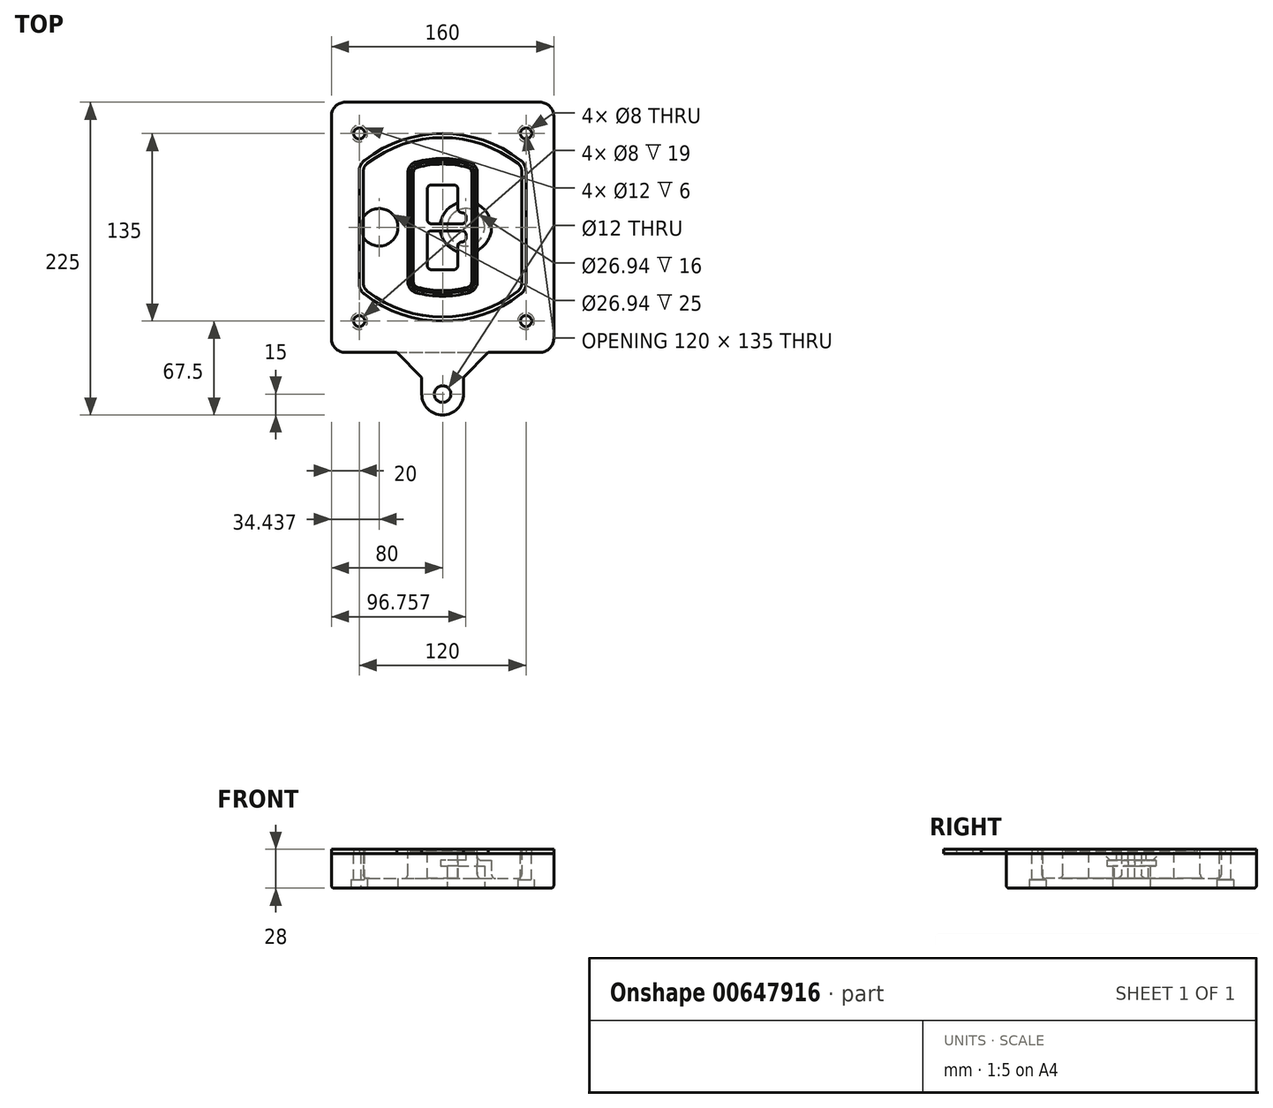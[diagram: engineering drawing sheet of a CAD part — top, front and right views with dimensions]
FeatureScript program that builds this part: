
annotation { "Feature Type Name" : "Feature", "Feature Type Description" : "" }
export const myFeature = defineFeature(function(context is Context, id is Id, definition is map)
    precondition{}
    {
        {
            var Q0;
            Q0=qCreatedBy(makeId("Top.planeOp"),FACE);
            var sketch = newSketch(context, id + "F0", { "sketchPlane" : qUnion([Q0])});
            skPoint(sketch, "E0.rect.middle", {"position": v(0, 0) * mm});
            skLineSegment(sketch, "E1.bottom", {"start": v(-70, -90) * mm, "end": v(70, -90) * mm});
            skLineSegment(sketch, "E1.top", {"start": v(-70, 90) * mm, "end": v(70, 90) * mm});
            skLineSegment(sketch, "E1.left", {"start": v(-80, -80) * mm, "end": v(-80, 80) * mm});
            skLineSegment(sketch, "E1.right", {"start": v(80, -80) * mm, "end": v(80, 80) * mm});
            skLineSegment(sketch, "E2", {"start": v(-80, 90) * mm, "end": v(80, -90) * mm, "construction": true});
            skLineSegment(sketch, "E3", {"start": v(80, 90) * mm, "end": v(-80, -90) * mm, "construction": true});
            skCircle(sketch, "E4", {"center": v(-60, 67.5) * mm, "radius": 4 * mm});
            skCircle(sketch, "E5", {"center": v(60, 67.5) * mm, "radius": 4 * mm});
            skCircle(sketch, "E6", {"center": v(60, -67.5) * mm, "radius": 4 * mm});
            skCircle(sketch, "E7", {"center": v(-60, -67.5) * mm, "radius": 4 * mm});
            skLineSegment(sketch, "E8", {"start": v(-60, 67.5) * mm, "end": v(60, 67.5) * mm, "construction": true});
            skLineSegment(sketch, "E9", {"start": v(60, 67.5) * mm, "end": v(60, -67.5) * mm, "construction": true});
            skLineSegment(sketch, "E10", {"start": v(60, -67.5) * mm, "end": v(-60, -67.5) * mm, "construction": true});
            skLineSegment(sketch, "E11", {"start": v(-60, -67.5) * mm, "end": v(-60, 67.5) * mm, "construction": true});
            skLineSegment(sketch, "E12", {"start": v(-60, 40.3) * mm, "end": v(-60, -40.3) * mm});
            skLineSegment(sketch, "E13", {"start": v(60, 40.3) * mm, "end": v(60, -40.3) * mm});
            skArc(sketch, "E14", {"start": v(56.15, 48.18) * mm, "mid": v(0, 67.5) * mm, "end": v(-56.15, 48.18) * mm});
            skArc(sketch, "E15", {"start": v(-56.15, -48.18) * mm, "mid": v(0, -67.5) * mm, "end": v(56.15, -48.18) * mm});
            skLineSegment(sketch, "E16", {"start": v(-60, 0) * mm, "end": v(60, 0) * mm, "construction": true});
            skPoint(sketch, "E17.visualSharp", {"position": v(-60, -45) * mm});
            skArc(sketch, "E17.filletArc", {"start": v(-60, -40.3) * mm, "mid": v(-58.99, -44.68) * mm, "end": v(-56.15, -48.18) * mm});
            skPoint(sketch, "E18.visualSharp", {"position": v(-60, 45) * mm});
            skArc(sketch, "E18.filletArc", {"start": v(-56.15, 48.18) * mm, "mid": v(-58.99, 44.68) * mm, "end": v(-60, 40.3) * mm});
            skPoint(sketch, "E19.visualSharp", {"position": v(60, 45) * mm});
            skArc(sketch, "E19.filletArc", {"start": v(60, 40.3) * mm, "mid": v(58.99, 44.68) * mm, "end": v(56.15, 48.18) * mm});
            skPoint(sketch, "E20.visualSharp", {"position": v(60, -45) * mm});
            skArc(sketch, "E20.filletArc", {"start": v(56.15, -48.18) * mm, "mid": v(58.99, -44.68) * mm, "end": v(60, -40.3) * mm});
            skPoint(sketch, "E21.visualSharp", {"position": v(-80, 90) * mm});
            skArc(sketch, "E21.filletArc", {"start": v(-70, 90) * mm, "mid": v(-77.07, 87.07) * mm, "end": v(-80, 80) * mm});
            skPoint(sketch, "E22.visualSharp", {"position": v(80, 90) * mm});
            skArc(sketch, "E22.filletArc", {"start": v(80, 80) * mm, "mid": v(77.07, 87.07) * mm, "end": v(70, 90) * mm});
            skPoint(sketch, "E23.visualSharp", {"position": v(80, -90) * mm});
            skArc(sketch, "E23.filletArc", {"start": v(70, -90) * mm, "mid": v(77.07, -87.07) * mm, "end": v(80, -80) * mm});
            skPoint(sketch, "E24.visualSharp", {"position": v(-80, -90) * mm});
            skArc(sketch, "E24.filletArc", {"start": v(-80, -80) * mm, "mid": v(-77.07, -87.07) * mm, "end": v(-70, -90) * mm});
            skArc(sketch, "E25.0", {"start": v(57, 40.3) * mm, "mid": v(56.3, 43.36) * mm, "end": v(54.3, 45.81) * mm});
            skLineSegment(sketch, "E25.1", {"start": v(57, 40.3) * mm, "end": v(57, -40.3) * mm});
            skArc(sketch, "E25.2", {"start": v(54.3, -45.81) * mm, "mid": v(56.3, -43.36) * mm, "end": v(57, -40.3) * mm});
            skArc(sketch, "E25.3", {"start": v(-54.3, -45.81) * mm, "mid": v(0, -64.5) * mm, "end": v(54.3, -45.81) * mm});
            skArc(sketch, "E25.4", {"start": v(-57, -40.3) * mm, "mid": v(-56.3, -43.36) * mm, "end": v(-54.3, -45.81) * mm});
            skArc(sketch, "E25.5", {"start": v(54.3, 45.81) * mm, "mid": v(0, 64.5) * mm, "end": v(-54.3, 45.81) * mm});
            skLineSegment(sketch, "E25.6", {"start": v(-57, 40.3) * mm, "end": v(-57, -40.3) * mm});
            skArc(sketch, "E25.7", {"start": v(-54.3, 45.81) * mm, "mid": v(-56.3, 43.36) * mm, "end": v(-57, 40.3) * mm});
            skArc(sketch, "E26.0", {"start": v(-58.62, 51.33) * mm, "mid": v(-62.58, 46.43) * mm, "end": v(-64, 40.3) * mm});
            skArc(sketch, "E26.1", {"start": v(58.62, 51.33) * mm, "mid": v(0, 71.5) * mm, "end": v(-58.62, 51.33) * mm});
            skArc(sketch, "E26.2", {"start": v(64, 40.3) * mm, "mid": v(62.58, 46.43) * mm, "end": v(58.62, 51.33) * mm});
            skLineSegment(sketch, "E26.3", {"start": v(64, 40.3) * mm, "end": v(64, -40.3) * mm});
            skArc(sketch, "E26.4", {"start": v(58.62, -51.33) * mm, "mid": v(62.58, -46.43) * mm, "end": v(64, -40.3) * mm});
            skLineSegment(sketch, "E26.5", {"start": v(-64, 40.3) * mm, "end": v(-64, -40.3) * mm});
            skArc(sketch, "E26.6", {"start": v(-58.62, -51.33) * mm, "mid": v(0, -71.5) * mm, "end": v(58.62, -51.33) * mm});
            skArc(sketch, "E26.7", {"start": v(-64, -40.3) * mm, "mid": v(-62.58, -46.43) * mm, "end": v(-58.62, -51.33) * mm});
            skSolve(sketch);
        }
        {
            var Q0;
            Q0=makeQuery(id+"F0.imprint","IMPRINT",FACE,{"disambiguationData":[TD([[makeQuery(id+"F0.imprint","IMPRINT",EDGE,{"derivedFrom":sQuery(id+"F0.wireOp",EDGE,"E1.bottom")}),1.0]])]});
            var Q1;
            Q1=makeQuery(id+"F0.imprint","IMPRINT",FACE,{"disambiguationData":[TD([[makeQuery(id+"F0.imprint","IMPRINT",EDGE,{"derivedFrom":sQuery(id+"F0.wireOp",EDGE,"E12")}),1.0]])]});
            var Q2;
            Q2=makeQuery(id+"F0.imprint","IMPRINT",FACE,{"disambiguationData":[TD([[makeQuery(id+"F0.imprint","IMPRINT",EDGE,{"derivedFrom":sQuery(id+"F0.wireOp",EDGE,"E25.0")}),1.0]])]});
            var Q3;
            Q3=makeQuery(id+"F0.imprint","IMPRINT",FACE,{"disambiguationData":[TD([[makeQuery(id+"F0.imprint","IMPRINT",EDGE,{"derivedFrom":sQuery(id+"F0.wireOp",EDGE,"E12")}),-1.0]])]});
            extrude(context, id + "F1", {"entities" : qUnion([Q0, Q1, Q2, Q3]), "oppositeDirection" : true, "depth" : 25 * mm});
        }
        {
            var Q0;
            Q0=makeQuery(id+"F0.imprint","IMPRINT",FACE,{"disambiguationData":[TD([[makeQuery(id+"F0.imprint","IMPRINT",EDGE,{"derivedFrom":sQuery(id+"F0.wireOp",EDGE,"E12")}),1.0]])]});
            extrude(context, id + "F2", {"entities" : qUnion([Q0]), "operationType" : NewBodyOperationType.ADD, "depth" : 3 * mm});
        }
        {
            var Q0;
            Q0=makeQuery(id+"F0.imprint","IMPRINT",FACE,{"disambiguationData":[TD([[makeQuery(id+"F0.imprint","IMPRINT",EDGE,{"derivedFrom":sQuery(id+"F0.wireOp",EDGE,"E25.0")}),1.0]])]});
            extrude(context, id + "F3", {"entities" : qUnion([Q0]), "operationType" : NewBodyOperationType.REMOVE, "oppositeDirection" : true, "depth" : 18 * mm});
        }
        {
            var Q0;
            Q0=makeQuery(id+"F2.opExtrude","CAP_FACE",FACE,{"disambiguationData":[OSD([sQuery(id+"F0.wireOp",EDGE,"E12"),sQuery(id+"F0.wireOp",EDGE,"E13"),sQuery(id+"F0.wireOp",EDGE,"E14"),sQuery(id+"F0.wireOp",EDGE,"E15"),sQuery(id+"F0.wireOp",EDGE,"E17.filletArc"),sQuery(id+"F0.wireOp",EDGE,"E18.filletArc"),sQuery(id+"F0.wireOp",EDGE,"E19.filletArc"),sQuery(id+"F0.wireOp",EDGE,"E20.filletArc"),sQuery(id+"F0.wireOp",EDGE,"E25.0"),sQuery(id+"F0.wireOp",EDGE,"E25.1"),sQuery(id+"F0.wireOp",EDGE,"E25.2"),sQuery(id+"F0.wireOp",EDGE,"E25.3"),sQuery(id+"F0.wireOp",EDGE,"E25.4"),sQuery(id+"F0.wireOp",EDGE,"E25.5"),sQuery(id+"F0.wireOp",EDGE,"E25.6"),sQuery(id+"F0.wireOp",EDGE,"E25.7")])],"isStart":false});
            var sketch = newSketch(context, id + "F4", { "sketchPlane" : qUnion([Q0])});
            skArc(sketch, "E27.0", {"start": v(-19.08, -46.97) * mm, "mid": v(0, -49.5) * mm, "end": v(19.08, -46.97) * mm});
            skArc(sketch, "E28.0", {"start": v(19.08, 46.97) * mm, "mid": v(0, 49.5) * mm, "end": v(-19.08, 46.97) * mm});
            skLineSegment(sketch, "E29", {"start": v(-25, 39.25) * mm, "end": v(-25, -39.25) * mm});
            skLineSegment(sketch, "E30", {"start": v(25, 39.25) * mm, "end": v(25, -39.25) * mm});
            skLineSegment(sketch, "E31", {"start": v(-25, 45.1) * mm, "end": v(25, 45.1) * mm, "construction": true});
            skLineSegment(sketch, "E32", {"start": v(-25, -45.1) * mm, "end": v(25, -45.1) * mm, "construction": true});
            skPoint(sketch, "E33.visualSharp", {"position": v(-25, 45.1) * mm});
            skArc(sketch, "E33.filletArc", {"start": v(-19.08, 46.97) * mm, "mid": v(-23.35, 44.11) * mm, "end": v(-25, 39.25) * mm});
            skPoint(sketch, "E34.visualSharp", {"position": v(25, 45.1) * mm});
            skArc(sketch, "E34.filletArc", {"start": v(25, 39.25) * mm, "mid": v(23.35, 44.11) * mm, "end": v(19.08, 46.97) * mm});
            skPoint(sketch, "E35.visualSharp", {"position": v(25, -45.1) * mm});
            skArc(sketch, "E35.filletArc", {"start": v(19.08, -46.97) * mm, "mid": v(23.35, -44.11) * mm, "end": v(25, -39.25) * mm});
            skPoint(sketch, "E36.visualSharp", {"position": v(-25, -45.1) * mm});
            skArc(sketch, "E36.filletArc", {"start": v(-25, -39.25) * mm, "mid": v(-23.35, -44.11) * mm, "end": v(-19.08, -46.97) * mm});
            skArc(sketch, "E37.0", {"start": v(54.3, 45.81) * mm, "mid": v(0, 64.5) * mm, "end": v(-54.3, 45.81) * mm});
            skArc(sketch, "E37.1", {"start": v(-54.3, 45.81) * mm, "mid": v(-56.3, 43.36) * mm, "end": v(-57, 40.3) * mm});
            skLineSegment(sketch, "E37.2", {"start": v(-57, 40.3) * mm, "end": v(-57, -40.3) * mm});
            skArc(sketch, "E37.3", {"start": v(-57, -40.3) * mm, "mid": v(-56.3, -43.36) * mm, "end": v(-54.3, -45.81) * mm});
            skArc(sketch, "E37.4", {"start": v(-54.3, -45.81) * mm, "mid": v(0, -64.5) * mm, "end": v(54.3, -45.81) * mm});
            skArc(sketch, "E37.5", {"start": v(54.3, -45.81) * mm, "mid": v(56.3, -43.36) * mm, "end": v(57, -40.3) * mm});
            skLineSegment(sketch, "E37.6", {"start": v(57, 40.3) * mm, "end": v(57, -40.3) * mm});
            skArc(sketch, "E37.7", {"start": v(57, 40.3) * mm, "mid": v(56.3, 43.36) * mm, "end": v(54.3, 45.81) * mm});
            skLineSegment(sketch, "E38.0", {"start": v(23, 39.25) * mm, "end": v(23, -39.25) * mm});
            skArc(sketch, "E38.1", {"start": v(18.56, -45.04) * mm, "mid": v(21.76, -42.9) * mm, "end": v(23, -39.25) * mm});
            skArc(sketch, "E38.2", {"start": v(-18.56, -45.04) * mm, "mid": v(0, -47.5) * mm, "end": v(18.56, -45.04) * mm});
            skArc(sketch, "E38.3", {"start": v(-23, -39.25) * mm, "mid": v(-21.76, -42.9) * mm, "end": v(-18.56, -45.04) * mm});
            skLineSegment(sketch, "E38.4", {"start": v(-23, 39.25) * mm, "end": v(-23, -39.25) * mm});
            skArc(sketch, "E38.5", {"start": v(23, 39.25) * mm, "mid": v(21.76, 42.9) * mm, "end": v(18.56, 45.04) * mm});
            skArc(sketch, "E38.6", {"start": v(-18.56, 45.04) * mm, "mid": v(-21.76, 42.9) * mm, "end": v(-23, 39.25) * mm});
            skArc(sketch, "E38.7", {"start": v(18.56, 45.04) * mm, "mid": v(0, 47.5) * mm, "end": v(-18.56, 45.04) * mm});
            skArc(sketch, "E39.0", {"start": v(21, 39.25) * mm, "mid": v(20.18, 41.68) * mm, "end": v(18.04, 43.1) * mm});
            skLineSegment(sketch, "E39.1", {"start": v(21, 39.25) * mm, "end": v(21, -39.25) * mm});
            skArc(sketch, "E39.2", {"start": v(18.04, -43.1) * mm, "mid": v(20.18, -41.68) * mm, "end": v(21, -39.25) * mm});
            skArc(sketch, "E39.3", {"start": v(-18.04, -43.1) * mm, "mid": v(0, -45.5) * mm, "end": v(18.04, -43.1) * mm});
            skArc(sketch, "E39.4", {"start": v(-21, -39.25) * mm, "mid": v(-20.18, -41.68) * mm, "end": v(-18.04, -43.1) * mm});
            skArc(sketch, "E39.5", {"start": v(18.04, 43.1) * mm, "mid": v(0, 45.5) * mm, "end": v(-18.04, 43.1) * mm});
            skLineSegment(sketch, "E39.6", {"start": v(-21, 39.25) * mm, "end": v(-21, -39.25) * mm});
            skArc(sketch, "E39.7", {"start": v(-18.04, 43.1) * mm, "mid": v(-20.18, 41.68) * mm, "end": v(-21, 39.25) * mm});
            skLineSegment(sketch, "E40", {"start": v(-25, 0) * mm, "end": v(25, 0) * mm, "construction": true});
            skLineSegment(sketch, "E41", {"start": v(-11, 5.5) * mm, "end": v(-11, 27.5) * mm});
            skLineSegment(sketch, "E42", {"start": v(-8, 30.5) * mm, "end": v(8, 30.5) * mm});
            skLineSegment(sketch, "E43", {"start": v(11, 27.5) * mm, "end": v(11, 13.5) * mm});
            skLineSegment(sketch, "E44", {"start": v(14, 10.5) * mm, "end": v(14, 10.5) * mm});
            skLineSegment(sketch, "E45", {"start": v(17, 7.5) * mm, "end": v(17, 5.5) * mm});
            skLineSegment(sketch, "E46", {"start": v(14, 2.5) * mm, "end": v(-8, 2.5) * mm});
            skPoint(sketch, "E47.visualSharp", {"position": v(-11, 30.5) * mm});
            skArc(sketch, "E47.filletArc", {"start": v(-8, 30.5) * mm, "mid": v(-10.12, 29.62) * mm, "end": v(-11, 27.5) * mm});
            skPoint(sketch, "E48.visualSharp", {"position": v(11, 30.5) * mm});
            skArc(sketch, "E48.filletArc", {"start": v(11, 27.5) * mm, "mid": v(10.12, 29.62) * mm, "end": v(8, 30.5) * mm});
            skPoint(sketch, "E49.visualSharp", {"position": v(11, 10.5) * mm});
            skArc(sketch, "E49.filletArc", {"start": v(11, 13.5) * mm, "mid": v(11.88, 11.38) * mm, "end": v(14, 10.5) * mm});
            skPoint(sketch, "E50.visualSharp", {"position": v(17, 10.5) * mm});
            skArc(sketch, "E50.filletArc", {"start": v(17, 7.5) * mm, "mid": v(16.12, 9.62) * mm, "end": v(14, 10.5) * mm});
            skPoint(sketch, "E51.visualSharp", {"position": v(17, 2.5) * mm});
            skArc(sketch, "E51.filletArc", {"start": v(14, 2.5) * mm, "mid": v(16.12, 3.38) * mm, "end": v(17, 5.5) * mm});
            skPoint(sketch, "E52.visualSharp", {"position": v(-11, 2.5) * mm});
            skArc(sketch, "E52.filletArc", {"start": v(-11, 5.5) * mm, "mid": v(-10.12, 3.38) * mm, "end": v(-8, 2.5) * mm});
            skLineSegment(sketch, "E53.0.MirrorCS", {"start": v(14, -2.5) * mm, "end": v(-8, -2.5) * mm});
            skArc(sketch, "E54.0.MirrorCS", {"start": v(-11, -5.5) * mm, "mid": v(-10.12, -3.38) * mm, "end": v(-8, -2.5) * mm});
            skLineSegment(sketch, "E55.0.MirrorCS", {"start": v(-11, -5.5) * mm, "end": v(-11, -27.5) * mm});
            skArc(sketch, "E56.0.MirrorCS", {"start": v(-8, -30.5) * mm, "mid": v(-10.12, -29.62) * mm, "end": v(-11, -27.5) * mm});
            skLineSegment(sketch, "E57.0.MirrorCS", {"start": v(-8, -30.5) * mm, "end": v(8, -30.5) * mm});
            skArc(sketch, "E58.0.MirrorCS", {"start": v(11, -27.5) * mm, "mid": v(10.12, -29.62) * mm, "end": v(8, -30.5) * mm});
            skLineSegment(sketch, "E59.0.MirrorCS", {"start": v(11, -27.5) * mm, "end": v(11, -13.5) * mm});
            skArc(sketch, "E60.0.MirrorCS", {"start": v(11, -13.5) * mm, "mid": v(11.88, -11.38) * mm, "end": v(14, -10.5) * mm});
            skArc(sketch, "E61.0.MirrorCS", {"start": v(17, -7.5) * mm, "mid": v(16.12, -9.62) * mm, "end": v(14, -10.5) * mm});
            skLineSegment(sketch, "E62.0.MirrorCS", {"start": v(17, -7.5) * mm, "end": v(17, -5.5) * mm});
            skArc(sketch, "E63.0.MirrorCS", {"start": v(14, -2.5) * mm, "mid": v(16.12, -3.38) * mm, "end": v(17, -5.5) * mm});
            skSolve(sketch);
        }
        {
            var Q0;
            Q0=makeQuery(id+"F4.imprint","IMPRINT",FACE,{"disambiguationData":[TD([[makeQuery(id+"F4.imprint","IMPRINT",EDGE,{"derivedFrom":sQuery(id+"F4.wireOp",EDGE,"E27.0")}),1.0]])]});
            var Q1;
            Q1=makeQuery(id+"F4.imprint","IMPRINT",FACE,{"disambiguationData":[TD([[makeQuery(id+"F4.imprint","IMPRINT",EDGE,{"derivedFrom":sQuery(id+"F4.wireOp",EDGE,"E38.0")}),-1.0]])]});
            var Q2;
            Q2=makeQuery(id+"F4.imprint","IMPRINT",FACE,{"disambiguationData":[TD([[makeQuery(id+"F4.imprint","IMPRINT",EDGE,{"derivedFrom":sQuery(id+"F4.wireOp",EDGE,"E39.0")}),1.0]])]});
            extrude(context, id + "F5", {"entities" : qUnion([Q0, Q1, Q2]), "operationType" : NewBodyOperationType.ADD, "endBound" : BoundingType.UP_TO_NEXT, "oppositeDirection" : true, "depth" : 25 * mm});
        }
        {
            var Q0;
            Q0=makeQuery(id+"F4.imprint","IMPRINT",FACE,{"disambiguationData":[TD([[makeQuery(id+"F4.imprint","IMPRINT",EDGE,{"derivedFrom":sQuery(id+"F4.wireOp",EDGE,"E38.0")}),-1.0]])]});
            extrude(context, id + "F6", {"entities" : qUnion([Q0]), "operationType" : NewBodyOperationType.REMOVE, "oppositeDirection" : true, "depth" : 2 * mm});
        }
        {
            var Q0;
            Q0=makeQuery(id+"F1.opExtrude","CAP_FACE",FACE,{"disambiguationData":[OSD([sQuery(id+"F0.wireOp",EDGE,"E1.bottom"),sQuery(id+"F0.wireOp",EDGE,"E1.top"),sQuery(id+"F0.wireOp",EDGE,"E1.left"),sQuery(id+"F0.wireOp",EDGE,"E1.right"),sQuery(id+"F0.wireOp",EDGE,"E4"),sQuery(id+"F0.wireOp",EDGE,"E5"),sQuery(id+"F0.wireOp",EDGE,"E6"),sQuery(id+"F0.wireOp",EDGE,"E7"),sQuery(id+"F0.wireOp",EDGE,"E21.filletArc"),sQuery(id+"F0.wireOp",EDGE,"E22.filletArc"),sQuery(id+"F0.wireOp",EDGE,"E23.filletArc"),sQuery(id+"F0.wireOp",EDGE,"E24.filletArc")])],"isStart":false});
            var sketch = newSketch(context, id + "F7", { "sketchPlane" : qUnion([Q0])});
            skCircle(sketch, "E64", {"center": v(16.76, 0) * mm, "radius": 13.47 * mm});
            skCircle(sketch, "E65", {"center": v(-45.56, 0) * mm, "radius": 13.47 * mm});
            skLineSegment(sketch, "E66", {"start": v(80, 0) * mm, "end": v(-80, 0) * mm});
            skCircle(sketch, "E67", {"center": v(16.76, 0) * mm, "radius": 18.47 * mm});
            skCircle(sketch, "E68", {"center": v(60, -67.5) * mm, "radius": 6 * mm});
            skCircle(sketch, "E69", {"center": v(-60, -67.5) * mm, "radius": 6 * mm});
            skCircle(sketch, "E70", {"center": v(-60, 67.5) * mm, "radius": 6 * mm});
            skCircle(sketch, "E71", {"center": v(60, 67.5) * mm, "radius": 6 * mm});
            skSolve(sketch);
        }
        {
            var Q0;
            {var subQ1=sQuery(id+"F7.wireOp",EDGE,"E66");var subQ4=sQuery(id+"F7.wireOp",EDGE,"E64");var subQ6=makeQuery(id+"F7.imprint","INTERSECT",VERTEX,{"disambiguationData":[OD(0.0)],"derivedFrom":[subQ4,subQ1]});Q0=makeQuery(id+"F7.imprint","IMPRINT",FACE,{"disambiguationData":[TD([[makeQuery(id+"F7.imprint","IMPRINT",EDGE,{"disambiguationData":[TD([[subQ6,-1.0]])],"derivedFrom":subQ4}),-1.0]])]});}
            var Q1;
            {var subQ0=sQuery(id+"F7.wireOp",EDGE,"E66");var subQ1=sQuery(id+"F7.wireOp",EDGE,"E64");var subQ3=makeQuery(id+"F7.imprint","INTERSECT",VERTEX,{"disambiguationData":[OD(0.0)],"derivedFrom":[subQ1,subQ0]});Q1=makeQuery(id+"F7.imprint","IMPRINT",FACE,{"disambiguationData":[TD([[makeQuery(id+"F7.imprint","IMPRINT",EDGE,{"disambiguationData":[TD([[subQ3,-1.0]])],"derivedFrom":subQ1}),1.0]])]});}
            var Q2;
            {var subQ0=sQuery(id+"F7.wireOp",EDGE,"E66");var subQ1=sQuery(id+"F7.wireOp",EDGE,"E64");var subQ3=makeQuery(id+"F7.imprint","INTERSECT",VERTEX,{"disambiguationData":[OD(0.0)],"derivedFrom":[subQ1,subQ0]});Q2=makeQuery(id+"F7.imprint","IMPRINT",FACE,{"disambiguationData":[TD([[makeQuery(id+"F7.imprint","IMPRINT",EDGE,{"disambiguationData":[TD([[subQ3,1.0]])],"derivedFrom":subQ1}),1.0]])]});}
            var Q3;
            {var subQ1=sQuery(id+"F7.wireOp",EDGE,"E66");var subQ4=sQuery(id+"F7.wireOp",EDGE,"E64");var subQ6=makeQuery(id+"F7.imprint","INTERSECT",VERTEX,{"disambiguationData":[OD(0.0)],"derivedFrom":[subQ4,subQ1]});Q3=makeQuery(id+"F7.imprint","IMPRINT",FACE,{"disambiguationData":[TD([[makeQuery(id+"F7.imprint","IMPRINT",EDGE,{"disambiguationData":[TD([[subQ6,1.0]])],"derivedFrom":subQ4}),-1.0]])]});}
            extrude(context, id + "F8", {"entities" : qUnion([Q0, Q1, Q2, Q3]), "operationType" : NewBodyOperationType.ADD, "oppositeDirection" : true, "depth" : 20 * mm});
        }
        {
            var Q0;
            {var subQ0=sQuery(id+"F7.wireOp",EDGE,"E66");var subQ1=sQuery(id+"F7.wireOp",EDGE,"E64");var subQ3=makeQuery(id+"F7.imprint","INTERSECT",VERTEX,{"disambiguationData":[OD(0.0)],"derivedFrom":[subQ1,subQ0]});Q0=makeQuery(id+"F7.imprint","IMPRINT",FACE,{"disambiguationData":[TD([[makeQuery(id+"F7.imprint","IMPRINT",EDGE,{"disambiguationData":[TD([[subQ3,-1.0]])],"derivedFrom":subQ1}),1.0]])]});}
            var Q1;
            {var subQ0=sQuery(id+"F7.wireOp",EDGE,"E66");var subQ1=sQuery(id+"F7.wireOp",EDGE,"E64");var subQ3=makeQuery(id+"F7.imprint","INTERSECT",VERTEX,{"disambiguationData":[OD(0.0)],"derivedFrom":[subQ1,subQ0]});Q1=makeQuery(id+"F7.imprint","IMPRINT",FACE,{"disambiguationData":[TD([[makeQuery(id+"F7.imprint","IMPRINT",EDGE,{"disambiguationData":[TD([[subQ3,1.0]])],"derivedFrom":subQ1}),1.0]])]});}
            extrude(context, id + "F9", {"entities" : qUnion([Q0, Q1]), "operationType" : NewBodyOperationType.REMOVE, "oppositeDirection" : true, "depth" : 16 * mm});
        }
        {
            var Q0;
            {var subQ0=sQuery(id+"F7.wireOp",EDGE,"E66");var subQ1=sQuery(id+"F7.wireOp",EDGE,"E65");var subQ3=makeQuery(id+"F7.imprint","INTERSECT",VERTEX,{"disambiguationData":[OD(0.0)],"derivedFrom":[subQ1,subQ0]});Q0=makeQuery(id+"F7.imprint","IMPRINT",FACE,{"disambiguationData":[TD([[makeQuery(id+"F7.imprint","IMPRINT",EDGE,{"disambiguationData":[TD([[subQ3,-1.0]])],"derivedFrom":subQ1}),1.0]])]});}
            var Q1;
            {var subQ0=sQuery(id+"F7.wireOp",EDGE,"E66");var subQ1=sQuery(id+"F7.wireOp",EDGE,"E65");var subQ3=makeQuery(id+"F7.imprint","INTERSECT",VERTEX,{"disambiguationData":[OD(0.0)],"derivedFrom":[subQ1,subQ0]});Q1=makeQuery(id+"F7.imprint","IMPRINT",FACE,{"disambiguationData":[TD([[makeQuery(id+"F7.imprint","IMPRINT",EDGE,{"disambiguationData":[TD([[subQ3,1.0]])],"derivedFrom":subQ1}),1.0]])]});}
            extrude(context, id + "F10", {"entities" : qUnion([Q0, Q1]), "operationType" : NewBodyOperationType.REMOVE, "oppositeDirection" : true, "depth" : 25 * mm});
        }
        {
            var Q0;
            Q0=makeQuery(id+"F7.imprint","IMPRINT",FACE,{"disambiguationData":[TD([[makeQuery(id+"F7.imprint","IMPRINT",EDGE,{"derivedFrom":sQuery(id+"F7.wireOp",EDGE,"E68")}),1.0]])]});
            var Q1;
            Q1=makeQuery(id+"F7.imprint","IMPRINT",FACE,{"disambiguationData":[TD([[makeQuery(id+"F7.imprint","IMPRINT",EDGE,{"derivedFrom":makeQuery(id+"F1.opExtrude","CAP_EDGE",EDGE,{"disambiguationData":[OSD([sQuery(id+"F0.wireOp",EDGE,"E5")])],"isStart":false})}),-1.0]])]});
            var Q2;
            Q2=makeQuery(id+"F7.imprint","IMPRINT",FACE,{"disambiguationData":[TD([[makeQuery(id+"F7.imprint","IMPRINT",EDGE,{"derivedFrom":sQuery(id+"F7.wireOp",EDGE,"E69")}),1.0]])]});
            var Q3;
            Q3=makeQuery(id+"F7.imprint","IMPRINT",FACE,{"disambiguationData":[TD([[makeQuery(id+"F7.imprint","IMPRINT",EDGE,{"derivedFrom":makeQuery(id+"F1.opExtrude","CAP_EDGE",EDGE,{"disambiguationData":[OSD([sQuery(id+"F0.wireOp",EDGE,"E4")])],"isStart":false})}),-1.0]])]});
            var Q4;
            Q4=makeQuery(id+"F7.imprint","IMPRINT",FACE,{"disambiguationData":[TD([[makeQuery(id+"F7.imprint","IMPRINT",EDGE,{"derivedFrom":sQuery(id+"F7.wireOp",EDGE,"E70")}),1.0]])]});
            var Q5;
            Q5=makeQuery(id+"F7.imprint","IMPRINT",FACE,{"disambiguationData":[TD([[makeQuery(id+"F7.imprint","IMPRINT",EDGE,{"derivedFrom":makeQuery(id+"F1.opExtrude","CAP_EDGE",EDGE,{"disambiguationData":[OSD([sQuery(id+"F0.wireOp",EDGE,"E7")])],"isStart":false})}),-1.0]])]});
            var Q6;
            Q6=makeQuery(id+"F7.imprint","IMPRINT",FACE,{"disambiguationData":[TD([[makeQuery(id+"F7.imprint","IMPRINT",EDGE,{"derivedFrom":sQuery(id+"F7.wireOp",EDGE,"E71")}),1.0]])]});
            var Q7;
            Q7=makeQuery(id+"F7.imprint","IMPRINT",FACE,{"disambiguationData":[TD([[makeQuery(id+"F7.imprint","IMPRINT",EDGE,{"derivedFrom":makeQuery(id+"F1.opExtrude","CAP_EDGE",EDGE,{"disambiguationData":[OSD([sQuery(id+"F0.wireOp",EDGE,"E6")])],"isStart":false})}),-1.0]])]});
            extrude(context, id + "F11", {"entities" : qUnion([Q0, Q1, Q2, Q3, Q4, Q5, Q6, Q7]), "operationType" : NewBodyOperationType.REMOVE, "oppositeDirection" : true, "depth" : 6 * mm});
        }
        {
            var Q0;
            Q0=makeQuery(id+"F9.boolean.opBoolean","COPY",FACE,{"derivedFrom":makeQuery(id+"F9.opExtrude","CAP_FACE",FACE,{"disambiguationData":[OSD([sQuery(id+"F7.wireOp",EDGE,"E64")])],"isStart":false})});
            var sketch = newSketch(context, id + "F12", { "sketchPlane" : qUnion([Q0])});
            skArc(sketch, "E72.0", {"start": v(11, 17.55) * mm, "mid": v(2.57, 11.82) * mm, "end": v(-1.54, 2.5) * mm});
            skArc(sketch, "E72.1", {"start": v(-1.54, -2.5) * mm, "mid": v(2.57, -11.82) * mm, "end": v(11, -17.55) * mm});
            skLineSegment(sketch, "E73", {"start": v(-1.54, -2.5) * mm, "end": v(14, -2.5) * mm});
            skLineSegment(sketch, "E74.0", {"start": v(14, 2.5) * mm, "end": v(-1.54, 2.5) * mm});
            skArc(sketch, "E74.1", {"start": v(14, 2.5) * mm, "mid": v(16.12, 3.38) * mm, "end": v(17, 5.5) * mm});
            skLineSegment(sketch, "E74.2", {"start": v(17, 7.5) * mm, "end": v(17, 5.5) * mm});
            skArc(sketch, "E74.3", {"start": v(17, 7.5) * mm, "mid": v(16.12, 9.62) * mm, "end": v(14, 10.5) * mm});
            skArc(sketch, "E74.4", {"start": v(11, 13.5) * mm, "mid": v(11.88, 11.38) * mm, "end": v(14, 10.5) * mm});
            skLineSegment(sketch, "E74.5", {"start": v(11, 17.55) * mm, "end": v(11, 13.5) * mm});
            skLineSegment(sketch, "E74.7", {"start": v(14, -2.5) * mm, "end": v(-1.54, -2.5) * mm});
            skArc(sketch, "E74.8", {"start": v(14, -2.5) * mm, "mid": v(16.12, -3.38) * mm, "end": v(17, -5.5) * mm});
            skLineSegment(sketch, "E74.9", {"start": v(17, -7.5) * mm, "end": v(17, -5.5) * mm});
            skArc(sketch, "E74.10", {"start": v(17, -7.5) * mm, "mid": v(16.12, -9.62) * mm, "end": v(14, -10.5) * mm});
            skArc(sketch, "E74.11", {"start": v(11, -13.5) * mm, "mid": v(11.88, -11.38) * mm, "end": v(14, -10.5) * mm});
            skLineSegment(sketch, "E74.12", {"start": v(11, -17.55) * mm, "end": v(11, -13.5) * mm});
            skPoint(sketch, "E75.orphan", {"position": v(11, -27.5) * mm});
            skPoint(sketch, "E76.orphan", {"position": v(-8, -2.5) * mm});
            skPoint(sketch, "E77.orphan", {"position": v(-8, 2.5) * mm});
            skPoint(sketch, "E78.orphan", {"position": v(11, 27.5) * mm});
            skSolve(sketch);
        }
        {
            var Q0;
            {var subQ7=sQuery(id+"F12.wireOp",EDGE,"E72.0");var subQ14=sQuery(id+"F12.wireOp",EDGE,"E72.1");var subQ16=sQuery(id+"F12.wireOp",EDGE,"E74.1");var subQ18=sQuery(id+"F12.wireOp",EDGE,"E74.8");Q0=qUnion([makeQuery(id+"F12.imprint","IMPRINT",FACE,{"disambiguationData":[TD([[makeQuery(id+"F12.imprint","IMPRINT",EDGE,{"derivedFrom":subQ7}),1.0]])]}),makeQuery(id+"F12.imprint","IMPRINT",FACE,{"disambiguationData":[TD([[makeQuery(id+"F12.imprint","IMPRINT",EDGE,{"derivedFrom":subQ14}),1.0]])]}),makeQuery(id+"F12.imprint","IMPRINT",FACE,{"disambiguationData":[TD([[makeQuery(id+"F12.imprint","IMPRINT",EDGE,{"derivedFrom":subQ16}),1.0]])]}),makeQuery(id+"F12.imprint","IMPRINT",FACE,{"disambiguationData":[TD([[makeQuery(id+"F12.imprint","IMPRINT",EDGE,{"derivedFrom":subQ18}),-1.0]])]})]);}
            var Q1;
            Q1=makeQuery(id+"F5.boolean.opBoolean","SPLIT",FACE,{"disambiguationData":[TD([makeQuery(id+"F5.opExtrude","SWEPT_FACE",FACE,{"disambiguationData":[OSD([sQuery(id+"F4.wireOp",EDGE,"E41")])]})])],"derivedFrom":makeQuery(id+"F3.boolean.opBoolean","COPY",FACE,{"derivedFrom":makeQuery(id+"F3.opExtrude","CAP_FACE",FACE,{"disambiguationData":[OSD([sQuery(id+"F0.wireOp",EDGE,"E25.0"),sQuery(id+"F0.wireOp",EDGE,"E25.1"),sQuery(id+"F0.wireOp",EDGE,"E25.2"),sQuery(id+"F0.wireOp",EDGE,"E25.3"),sQuery(id+"F0.wireOp",EDGE,"E25.4"),sQuery(id+"F0.wireOp",EDGE,"E25.5"),sQuery(id+"F0.wireOp",EDGE,"E25.6"),sQuery(id+"F0.wireOp",EDGE,"E25.7")])],"isStart":false})})});
            extrude(context, id + "F13", {"entities" : qUnion([Q0]), "operationType" : NewBodyOperationType.REMOVE, "endBound" : BoundingType.UP_TO_SURFACE, "endBoundEntityFace" : qUnion([Q1]), "depth" : 25 * mm});
        }
        {
            var Q0;
            Q0=makeQuery(id+"F3.boolean.opBoolean","COPY",EDGE,{"derivedFrom":makeQuery(id+"F3.opExtrude","CAP_EDGE",EDGE,{"disambiguationData":[OSD([sQuery(id+"F0.wireOp",EDGE,"E25.6")])],"isStart":false})});
            var Q1;
            Q1=makeQuery(id+"F8.boolean.opBoolean","INTERSECT",EDGE,{"derivedFrom":[makeQuery(id+"F5.opExtrude","SWEPT_FACE",FACE,{"disambiguationData":[OSD([sQuery(id+"F4.wireOp",EDGE,"E30")])]}),makeQuery(id+"F8.opExtrude","CAP_FACE",FACE,{"disambiguationData":[OSD([sQuery(id+"F7.wireOp",EDGE,"E67")])],"isStart":false})]});
            var Q2;
            Q2=makeQuery(id+"F8.boolean.opBoolean","INTERSECT",EDGE,{"disambiguationData":[OD(1.0)],"derivedFrom":[makeQuery(id+"F5.opExtrude","SWEPT_FACE",FACE,{"disambiguationData":[OSD([sQuery(id+"F4.wireOp",EDGE,"E30")])]}),makeQuery(id+"F8.opExtrude","SWEPT_FACE",FACE,{"disambiguationData":[OSD([sQuery(id+"F7.wireOp",EDGE,"E67")])]})]});
            var Q3;
            {var subQ0=sQuery(id+"F4.wireOp",EDGE,"E30");Q3=makeQuery(id+"F8.boolean.opBoolean","SPLIT",EDGE,{"disambiguationData":[TD([makeQuery(id+"F5.opExtrude","SWEPT_FACE",FACE,{"disambiguationData":[OSD([sQuery(id+"F4.wireOp",EDGE,"E35.filletArc")])]})])],"derivedFrom":makeQuery(id+"F5.opExtrude","CAP_EDGE",EDGE,{"disambiguationData":[OSD([subQ0])],"isStart":false})});}
            var Q4;
            {var subQ0=sQuery(id+"F0.wireOp",EDGE,"E25.7");var subQ1=sQuery(id+"F0.wireOp",EDGE,"E25.1");var subQ2=sQuery(id+"F0.wireOp",EDGE,"E25.6");var subQ3=sQuery(id+"F0.wireOp",EDGE,"E25.5");var subQ4=sQuery(id+"F0.wireOp",EDGE,"E25.4");var subQ5=sQuery(id+"F0.wireOp",EDGE,"E25.0");var subQ6=sQuery(id+"F0.wireOp",EDGE,"E25.2");var subQ7=sQuery(id+"F0.wireOp",EDGE,"E25.3");Q4=makeQuery(id+"F8.boolean.opBoolean","INTERSECT",EDGE,{"derivedFrom":[makeQuery(id+"F5.boolean.opBoolean","SPLIT",FACE,{"disambiguationData":[TD([makeQuery(id+"F2.opExtrude","SWEPT_FACE",FACE,{"disambiguationData":[OSD([subQ5])]})])],"derivedFrom":makeQuery(id+"F3.boolean.opBoolean","COPY",FACE,{"derivedFrom":makeQuery(id+"F3.opExtrude","CAP_FACE",FACE,{"disambiguationData":[OSD([subQ5,subQ1,subQ6,subQ7,subQ4,subQ3,subQ2,subQ0])],"isStart":false})})}),makeQuery(id+"F8.opExtrude","SWEPT_FACE",FACE,{"disambiguationData":[OSD([sQuery(id+"F7.wireOp",EDGE,"E67")])]})]});}
            var Q5;
            Q5=makeQuery(id+"F8.boolean.opBoolean","INTERSECT",EDGE,{"disambiguationData":[OD(0.0)],"derivedFrom":[makeQuery(id+"F5.opExtrude","SWEPT_FACE",FACE,{"disambiguationData":[OSD([sQuery(id+"F4.wireOp",EDGE,"E30")])]}),makeQuery(id+"F8.opExtrude","SWEPT_FACE",FACE,{"disambiguationData":[OSD([sQuery(id+"F7.wireOp",EDGE,"E67")])]})]});
            fillet(context, id + "F14", {"entities" : qUnion([Q0, Q1, Q2, Q3, Q4, Q5]), "radius" : 3 * mm, "tangentPropagation" : true, "allowEdgeOverflow" : false});
        }
        {
            var Q0;
            Q0=makeQuery(id+"F1.opExtrude","CAP_EDGE",EDGE,{"disambiguationData":[OSD([sQuery(id+"F0.wireOp",EDGE,"E1.bottom")])],"isStart":false});
            fillet(context, id + "F15", {"entities" : qUnion([Q0]), "radius" : 2 * mm, "tangentPropagation" : true, "allowEdgeOverflow" : false});
        }
        {
            var Q0;
            {var subQ0=sQuery(id+"F0.wireOp",EDGE,"E21.filletArc");var subQ1=sQuery(id+"F0.wireOp",EDGE,"E7");var subQ2=sQuery(id+"F0.wireOp",EDGE,"E6");var subQ3=sQuery(id+"F0.wireOp",EDGE,"E5");var subQ4=sQuery(id+"F0.wireOp",EDGE,"E4");var subQ5=sQuery(id+"F0.wireOp",EDGE,"E22.filletArc");var subQ6=sQuery(id+"F0.wireOp",EDGE,"E1.bottom");var subQ7=sQuery(id+"F0.wireOp",EDGE,"E1.right");var subQ8=sQuery(id+"F0.wireOp",EDGE,"E1.top");var subQ9=sQuery(id+"F0.wireOp",EDGE,"E1.left");var subQ10=sQuery(id+"F0.wireOp",EDGE,"E23.filletArc");var subQ11=sQuery(id+"F0.wireOp",EDGE,"E24.filletArc");Q0=makeQuery(id+"F2.boolean.opBoolean","SPLIT",FACE,{"disambiguationData":[TD([makeQuery(id+"F1.opExtrude","SWEPT_FACE",FACE,{"disambiguationData":[OSD([subQ6])]})])],"derivedFrom":makeQuery(id+"F1.opExtrude","CAP_FACE",FACE,{"disambiguationData":[OSD([subQ6,subQ8,subQ9,subQ7,subQ4,subQ3,subQ2,subQ1,subQ0,subQ5,subQ10,subQ11])],"isStart":true})});}
            var sketch = newSketch(context, id + "F16", { "sketchPlane" : qUnion([Q0])});
            skLineSegment(sketch, "E79", {"start": v(-33, 90) * mm, "end": v(-15, 108) * mm});
            skLineSegment(sketch, "E80", {"start": v(-15, 108) * mm, "end": v(-15, 120) * mm});
            skLineSegment(sketch, "E81", {"start": v(0, 90) * mm, "end": v(0, 120) * mm, "construction": true});
            skCircle(sketch, "E82", {"center": v(0, 120) * mm, "radius": 6 * mm});
            skLineSegment(sketch, "E83.MirrorCS", {"start": v(15, 108) * mm, "end": v(15, 120) * mm});
            skLineSegment(sketch, "E84.MirrorCS", {"start": v(33, 90) * mm, "end": v(15, 108) * mm});
            skArc(sketch, "E85", {"start": v(15, 120) * mm, "mid": v(0, 135) * mm, "end": v(-15, 120) * mm});
            skLineSegment(sketch, "E86", {"start": v(-80, 0) * mm, "end": v(80, 0) * mm, "construction": true});
            skArc(sketch, "E87.MirrorCS", {"start": v(-15, 120) * mm, "mid": v(0, 135) * mm, "end": v(15, 120) * mm});
            skLineSegment(sketch, "E88.MirrorCS", {"start": v(80, 0) * mm, "end": v(-80, 0) * mm, "construction": true});
            skLineSegment(sketch, "E89.MirrorCS", {"start": v(-15, -108) * mm, "end": v(-15, -120) * mm});
            skLineSegment(sketch, "E90.MirrorCS", {"start": v(15, -108) * mm, "end": v(15, -120) * mm});
            skCircle(sketch, "E91.MirrorC", {"center": v(0, -120) * mm, "radius": 6 * mm});
            skArc(sketch, "E92.MirrorCS", {"start": v(15, -120) * mm, "mid": v(0, -135) * mm, "end": v(-15, -120) * mm});
            skLineSegment(sketch, "E93.MirrorCS", {"start": v(-33, -90) * mm, "end": v(-15, -108) * mm});
            skLineSegment(sketch, "E94.MirrorCS", {"start": v(33, -90) * mm, "end": v(15, -108) * mm});
            skArc(sketch, "E95.MirrorCS", {"start": v(-15, -120) * mm, "mid": v(0, -135) * mm, "end": v(15, -120) * mm});
            skLineSegment(sketch, "E96.MirrorCS", {"start": v(0, -90) * mm, "end": v(0, -120) * mm, "construction": true});
            skSolve(sketch);
        }
        {
            var Q0;
            {var subQ0=sQuery(id+"F16.wireOp",EDGE,"E94.MirrorCS");Q0=makeQuery(id+"F16.imprint","IMPRINT",FACE,{"disambiguationData":[TD([[makeQuery(id+"F16.imprint","IMPRINT",EDGE,{"derivedFrom":subQ0}),-1.0]])]});}
            var Q1;
            Q1=makeQuery(id+"F16.imprint","IMPRINT",FACE,{"disambiguationData":[TD([[makeQuery(id+"F16.imprint","IMPRINT",EDGE,{"derivedFrom":sQuery(id+"F16.wireOp",EDGE,"E87.MirrorCS")}),-1.0]])]});
            var Q2;
            Q2=makeQuery(id+"F16.imprint","IMPRINT",FACE,{"disambiguationData":[TD([[makeQuery(id+"F16.imprint","IMPRINT",EDGE,{"derivedFrom":makeQuery(id+"F1.opExtrude","CAP_EDGE",EDGE,{"disambiguationData":[OSD([sQuery(id+"F0.wireOp",EDGE,"E1.left")])],"isStart":true})}),-1.0]])]});
            var Q3;
            Q3=makeQuery(id+"F2.opExtrude","CAP_FACE",FACE,{"disambiguationData":[OSD([sQuery(id+"F0.wireOp",EDGE,"E12"),sQuery(id+"F0.wireOp",EDGE,"E13"),sQuery(id+"F0.wireOp",EDGE,"E14"),sQuery(id+"F0.wireOp",EDGE,"E15"),sQuery(id+"F0.wireOp",EDGE,"E17.filletArc"),sQuery(id+"F0.wireOp",EDGE,"E18.filletArc"),sQuery(id+"F0.wireOp",EDGE,"E19.filletArc"),sQuery(id+"F0.wireOp",EDGE,"E20.filletArc"),sQuery(id+"F0.wireOp",EDGE,"E25.0"),sQuery(id+"F0.wireOp",EDGE,"E25.1"),sQuery(id+"F0.wireOp",EDGE,"E25.2"),sQuery(id+"F0.wireOp",EDGE,"E25.3"),sQuery(id+"F0.wireOp",EDGE,"E25.4"),sQuery(id+"F0.wireOp",EDGE,"E25.5"),sQuery(id+"F0.wireOp",EDGE,"E25.6"),sQuery(id+"F0.wireOp",EDGE,"E25.7")])],"isStart":false});
            extrude(context, id + "F17", {"entities" : qUnion([Q0, Q1, Q2]), "endBound" : BoundingType.UP_TO_SURFACE, "depth" : 25 * mm, "endBoundEntityFace" : qUnion([Q3]), "offsetDistance" : 25 * mm});
        }
    });
